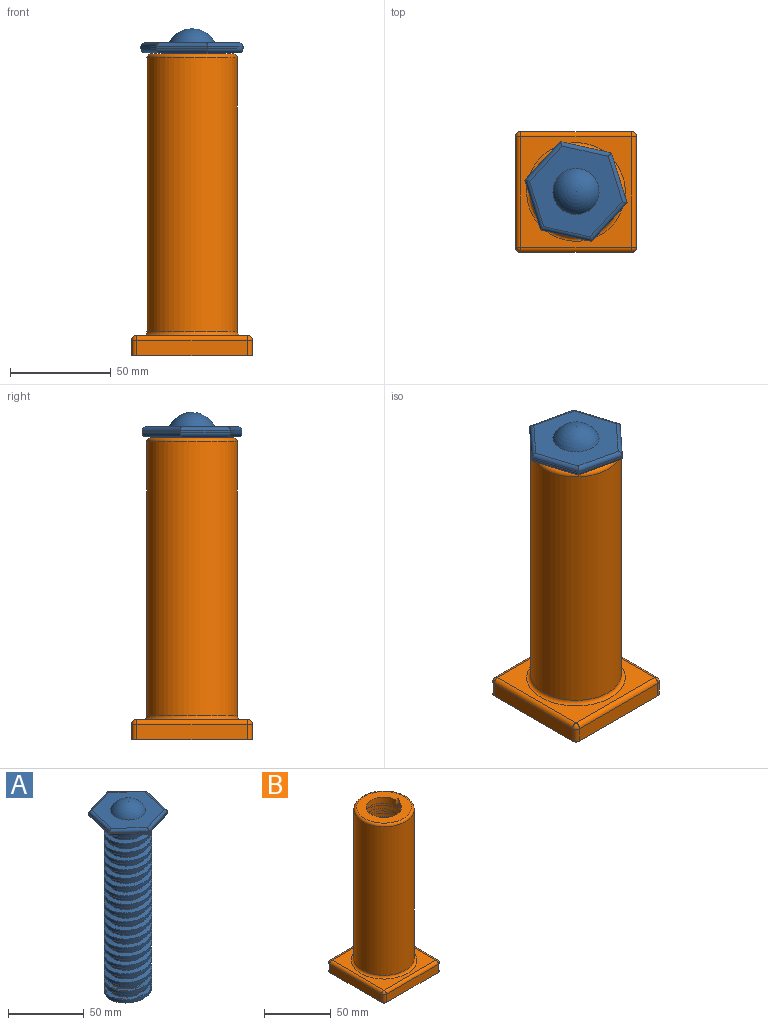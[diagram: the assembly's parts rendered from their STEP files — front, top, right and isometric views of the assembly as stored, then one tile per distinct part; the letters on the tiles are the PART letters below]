
ASSEMBLY  parts=2 mates=1
PART A: 28 faces, bbox 50x51.1x154.7 mm
  f0: sphere r=12.7mm, area 39.9mm2, adj f1,f14
  f1: cylinder r=12.7mm len=140mm, axis (0,0,-1), area 6320.5mm2, adj f0,f2,f3,f4,f5
  f2: plane 29.02x28.77mm, normal (0,0,-1), area 629.9mm2, adj f1,f4,f5,f6
  f3: plane 4x3mm, normal (0,1,0), area 9.8mm2, adj f1,f4,f5,f6
  f4: bspline ~140.75x36.26mm, area 5484.8mm2, adj f1,f2,f3,f6
  f5: bspline ~138.42x36.26mm, area 5408.5mm2, adj f1,f2,f3,f6
  f6: cylinder r=15.7mm len=139.25mm, axis (0,0,-1), area 3760.7mm2, adj f2,f3,f4,f5
  f7: plane 25.35x5.68mm, normal (0.98,-0.22,0), area 26mm2, adj f8,f12,f18,f24
  f8: plane 19.11x17.6mm, normal (0.68,0.74,0), area 26mm2, adj f7,f9,f16,f22
  f9: plane 24.8x7.75mm, normal (-0.3,0.95,0), area 26mm2, adj f8,f10,f17,f23
  f10: plane 25.35x5.68mm, normal (-0.98,0.22,0), area 26mm2, adj f9,f11,f19,f25
  f11: plane 19.11x17.6mm, normal (-0.68,-0.74,0), area 26mm2, adj f10,f12,f21,f27
  f12: plane 24.8x7.75mm, normal (0.3,-0.95,0), area 26mm2, adj f7,f11,f20,f26
  f13: plane 46.2x45.19mm, normal (0,0,1), area 1044.1mm2, adj f15,f22,f23,f24,f25,f26,f27
  f14: plane 46.2x45.19mm, normal (0,0,-1), area 949.9mm2, adj f0,f16,f17,f18,f19,f20,f21
  f15: sphere r=12.7mm, area 574.5mm2, adj f13
  f16: cylinder r=2mm len=20.47mm, axis (-0.74,0.68,0), area 78mm2, adj f8,f14,f17,f18
  f17: cylinder r=2mm len=25.39mm, axis (-0.95,-0.3,0), area 78mm2, adj f9,f14,f16,f19
  f18: cylinder r=2mm len=25.79mm, axis (0.22,0.98,0), area 78mm2, adj f7,f14,f16,f20
  f19: cylinder r=2mm len=25.79mm, axis (-0.22,-0.98,0), area 78mm2, adj f10,f14,f17,f21
  f20: cylinder r=2mm len=25.39mm, axis (0.95,0.3,0), area 78mm2, adj f12,f14,f18,f21
  f21: cylinder r=2mm len=20.47mm, axis (0.74,-0.68,0), area 78mm2, adj f11,f14,f19,f20
  f22: cylinder r=2mm len=20.47mm, axis (0.74,-0.68,0), area 78mm2, adj f8,f13,f23,f24
  f23: cylinder r=2mm len=25.39mm, axis (0.95,0.3,0), area 78mm2, adj f9,f13,f22,f25
  f24: cylinder r=2mm len=25.79mm, axis (-0.22,-0.98,0), area 78mm2, adj f7,f13,f22,f26
  f25: cylinder r=2mm len=25.79mm, axis (0.22,0.98,0), area 78mm2, adj f10,f13,f23,f27
  f26: cylinder r=2mm len=25.39mm, axis (-0.95,-0.3,0), area 78mm2, adj f12,f13,f24,f27
  f27: cylinder r=2mm len=20.47mm, axis (-0.74,0.68,0), area 78mm2, adj f11,f13,f25,f26
PART B: 27 faces, bbox 60x60x150 mm
  f0: plane 41x41mm, normal (0,0,1), area 768.1mm2, adj f2,f4,f26
  f1: cylinder r=22.5mm len=136mm, axis (0,0,-1), area 19226.5mm2, adj f25,f26
  f2: cylinder r=13.2mm len=140mm, axis (0,0,-1), area 3469.5mm2, adj f0,f4,f11
  f3: cylinder r=16.2mm len=139.67mm, axis (0,0,-1), area 5863.3mm2, adj f4,f11
  f4: plane 4.36x3mm, normal (0,-1,0), area 11.7mm2, adj f0,f2,f3
  f5: plane 55x55mm, normal (0,0,1), area 1139.3mm2, adj f15,f16,f20,f21,f25
  f6: plane 55x7.5mm, normal (1,0,0), area 412.5mm2, adj f10,f14,f20,f23
  f7: plane 55x7.5mm, normal (0,1,0), area 412.5mm2, adj f10,f17,f21,f23
  f8: plane 55x7.5mm, normal (-1,0,0), area 412.5mm2, adj f10,f12,f16,f17
  f9: plane 55x7.5mm, normal (0,-1,0), area 412.5mm2, adj f10,f12,f14,f15
  f10: plane 60x60mm, normal (0,0,-1), area 3071.8mm2, adj f6,f7,f8,f9,f12,f14,f17,f23
  f11: plane 31.56x29.6mm, normal (0,0,1), area 203.7mm2, adj f2,f3,f24
  f12: cylinder r=2.5mm len=7.5mm, axis (0,0,-1), area 29.5mm2, adj f8,f9,f10,f13
  f13: sphere r=2.5mm, area 9.8mm2, adj f12,f15,f16
  f14: cylinder r=2.5mm len=7.5mm, axis (0,0,1), area 29.5mm2, adj f6,f9,f10,f18
  f15: cylinder r=2.5mm len=55mm, axis (1,0,0), area 216mm2, adj f5,f9,f13,f18
  f16: cylinder r=2.5mm len=55mm, axis (0,-1,0), area 216mm2, adj f5,f8,f13,f19
  f17: cylinder r=2.5mm len=7.5mm, axis (0,0,1), area 29.5mm2, adj f7,f8,f10,f19
  f18: sphere r=2.5mm, area 9.8mm2, adj f14,f15,f20
  f19: sphere r=2.5mm, area 9.8mm2, adj f16,f17,f21
  f20: cylinder r=2.5mm len=55mm, axis (0,1,0), area 216mm2, adj f5,f6,f18,f22
  f21: cylinder r=2.5mm len=55mm, axis (-1,0,0), area 216mm2, adj f5,f7,f19,f22
  f22: sphere r=2.5mm, area 9.8mm2, adj f20,f21,f23
  f23: cylinder r=2.5mm len=7.5mm, axis (0,0,-1), area 29.5mm2, adj f6,f7,f10,f22
  f24: cylinder r=12.9mm len=25.8mm, axis (0,0,1), area 810.5mm2, adj f10,f11
  f25: torus R=24.5mm, axis (0,0,1), area 458.5mm2, adj f1,f5
  f26: torus R=20.5mm, axis (0,0,1), area 429.8mm2, adj f0,f1
PLACE A rot(axis=(0,0,1),90deg) t=(-52.85,1.23,-24.34)mm
PLACE B t=(-52.85,1.23,-24.34)mm fixed
MATE cylindrical B.f2 <-> A.f1  axis (0,0,1) through (-52.85,1.23,115.66)mm
